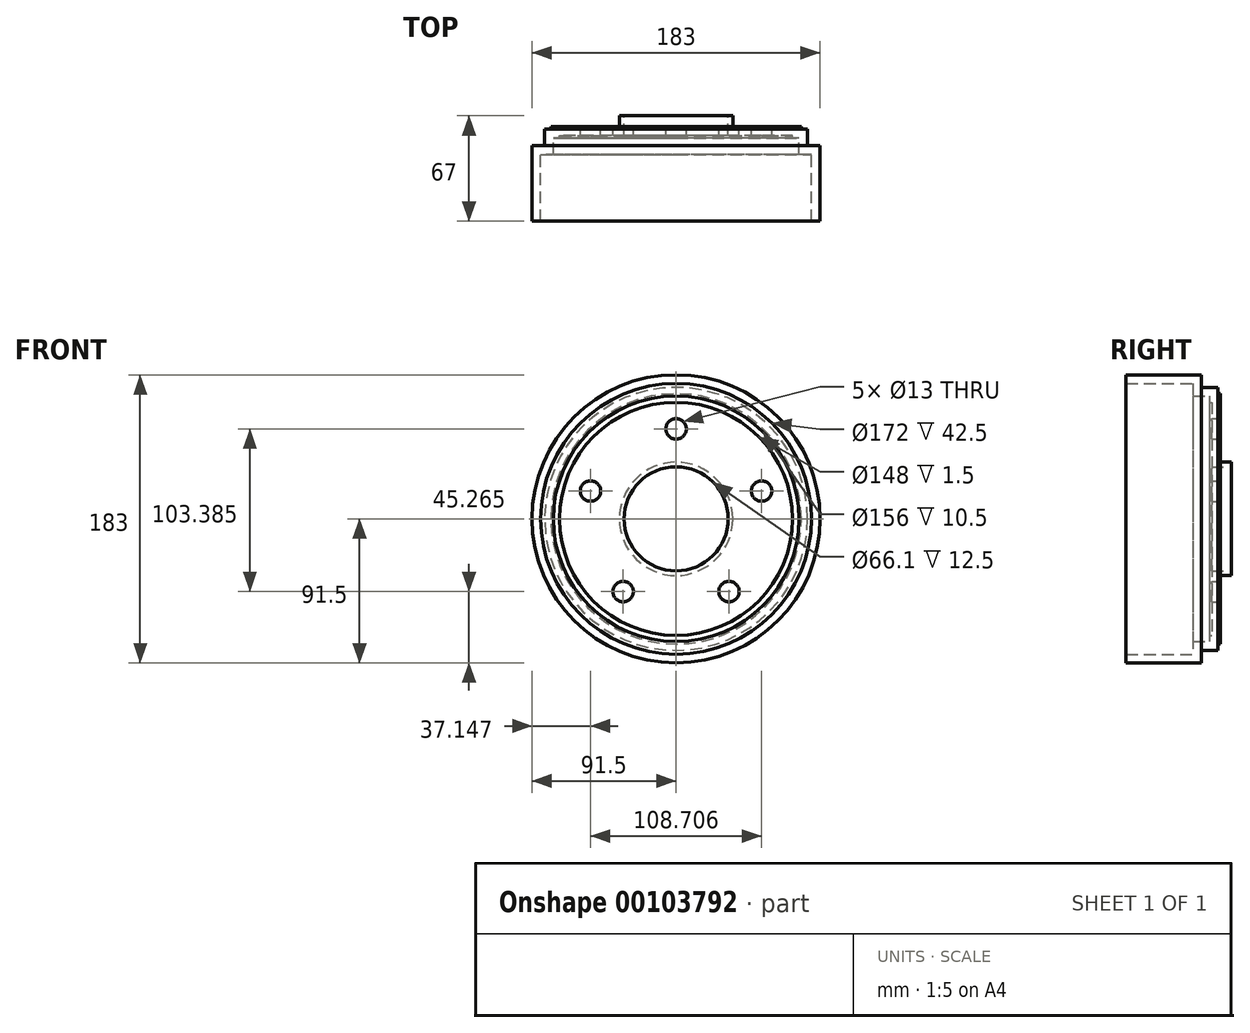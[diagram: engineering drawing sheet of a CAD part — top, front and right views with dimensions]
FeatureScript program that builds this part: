
annotation { "Feature Type Name" : "Feature", "Feature Type Description" : "" }
export const myFeature = defineFeature(function(context is Context, id is Id, definition is map)
    precondition{}
    {
        {
            var Q0;
            Q0=qCreatedBy(makeId("Top.planeOp"),FACE);
            var sketch = newSketch(context, id + "F0", { "sketchPlane" : qUnion([Q0])});
            skLineSegment(sketch, "E0", {"start": v(-86, -71.5) * mm, "end": v(-86, -29) * mm, "construction": true});
            skLineSegment(sketch, "E1", {"start": v(86, -71.5) * mm, "end": v(86, -29) * mm});
            skLineSegment(sketch, "E2", {"start": v(86, -29) * mm, "end": v(78, -29) * mm});
            skLineSegment(sketch, "E3", {"start": v(78, -29) * mm, "end": v(78, -18.5) * mm});
            skLineSegment(sketch, "E4", {"start": v(78, -18.5) * mm, "end": v(74, -18.5) * mm});
            skLineSegment(sketch, "E5", {"start": v(74, -18.5) * mm, "end": v(74, -17) * mm});
            skLineSegment(sketch, "E6", {"start": v(74, -17) * mm, "end": v(30.5, -17) * mm});
            skLineSegment(sketch, "E7", {"start": v(30.5, -17) * mm, "end": v(30.5, -10) * mm});
            skLineSegment(sketch, "E8", {"start": v(30.5, -10) * mm, "end": v(27.55, -10) * mm});
            skLineSegment(sketch, "E9", {"start": v(27.55, -10) * mm, "end": v(27.55, 0) * mm});
            skLineSegment(sketch, "E10", {"start": v(-27.55, 0) * mm, "end": v(-27.55, -10) * mm, "construction": true});
            skLineSegment(sketch, "E11", {"start": v(-27.55, -10) * mm, "end": v(-30.5, -10) * mm, "construction": true});
            skLineSegment(sketch, "E12", {"start": v(-30.5, -10) * mm, "end": v(-30.5, -17) * mm, "construction": true});
            skLineSegment(sketch, "E13", {"start": v(-30.5, -17) * mm, "end": v(-74, -17) * mm, "construction": true});
            skLineSegment(sketch, "E14", {"start": v(-74, -17) * mm, "end": v(-74, -18.5) * mm, "construction": true});
            skLineSegment(sketch, "E15", {"start": v(-74, -18.5) * mm, "end": v(-78, -18.5) * mm, "construction": true});
            skLineSegment(sketch, "E16", {"start": v(-78, -18.5) * mm, "end": v(-78, -29) * mm, "construction": true});
            skLineSegment(sketch, "E17", {"start": v(-78, -29) * mm, "end": v(-86, -29) * mm, "construction": true});
            skLineSegment(sketch, "E18", {"start": v(86, -71.5) * mm, "end": v(91.5, -71.5) * mm});
            skLineSegment(sketch, "E19", {"start": v(91.5, -71.5) * mm, "end": v(91.5, -23.5) * mm});
            skLineSegment(sketch, "E20", {"start": v(91.5, -23.5) * mm, "end": v(83.5, -23.5) * mm});
            skLineSegment(sketch, "E21", {"start": v(83.5, -23.5) * mm, "end": v(83.5, -13) * mm});
            skLineSegment(sketch, "E22", {"start": v(83.5, -13) * mm, "end": v(79.5, -13) * mm});
            skLineSegment(sketch, "E23", {"start": v(79.5, -13) * mm, "end": v(79.5, -11.5) * mm});
            skLineSegment(sketch, "E24", {"start": v(79.5, -11.5) * mm, "end": v(36, -11.5) * mm});
            skLineSegment(sketch, "E25", {"start": v(36, -11.5) * mm, "end": v(36, -4.5) * mm});
            skLineSegment(sketch, "E26", {"start": v(36, -4.5) * mm, "end": v(33.05, -4.5) * mm});
            skLineSegment(sketch, "E27", {"start": v(33.05, -4.5) * mm, "end": v(33.05, 5.5) * mm});
            skLineSegment(sketch, "E28", {"start": v(-33.05, 5.5) * mm, "end": v(-33.05, -4.5) * mm, "construction": true});
            skLineSegment(sketch, "E29", {"start": v(-33.05, -4.5) * mm, "end": v(-36, -4.5) * mm, "construction": true});
            skLineSegment(sketch, "E30", {"start": v(-36, -4.5) * mm, "end": v(-36, -11.5) * mm, "construction": true});
            skLineSegment(sketch, "E31", {"start": v(-36, -11.5) * mm, "end": v(-79.5, -11.5) * mm, "construction": true});
            skLineSegment(sketch, "E32", {"start": v(-79.5, -11.5) * mm, "end": v(-79.5, -13) * mm, "construction": true});
            skLineSegment(sketch, "E33", {"start": v(-79.5, -13) * mm, "end": v(-83.5, -13) * mm, "construction": true});
            skLineSegment(sketch, "E34", {"start": v(-83.5, -13) * mm, "end": v(-83.5, -23.5) * mm, "construction": true});
            skLineSegment(sketch, "E35", {"start": v(-83.5, -23.5) * mm, "end": v(-91.5, -23.5) * mm, "construction": true});
            skLineSegment(sketch, "E36", {"start": v(-91.5, -23.5) * mm, "end": v(-91.5, -71.5) * mm, "construction": true});
            skLineSegment(sketch, "E37", {"start": v(-91.5, -71.5) * mm, "end": v(-86, -71.5) * mm, "construction": true});
            skLineSegment(sketch, "E38", {"start": v(0, 0) * mm, "end": v(27.55, 0) * mm});
            skLineSegment(sketch, "E39", {"start": v(33.05, 5.5) * mm, "end": v(0, 5.5) * mm});
            skLineSegment(sketch, "E40", {"start": v(0, 5.5) * mm, "end": v(0, 0) * mm});
            skLineSegment(sketch, "E41", {"start": v(-27.55, 0) * mm, "end": v(0, 0) * mm, "construction": true});
            skLineSegment(sketch, "E42", {"start": v(-33.05, 5.5) * mm, "end": v(0, 5.5) * mm, "construction": true});
            skSolve(sketch);
        }
        {
            var Q0;
            Q0=makeQuery(id+"F0.imprint","IMPRINT",FACE,{"disambiguationData":[TD([[makeQuery(id+"F0.imprint","IMPRINT",EDGE,{"derivedFrom":sQuery(id+"F0.wireOp",EDGE,"E1")}),-1.0]])]});
            var Q1;
            Q1=sQuery(id+"F0.wireOp",EDGE,"E40");
            revolve(context, id + "F1", {"entities" : qUnion([Q0]), "axis" : qUnion([Q1]), "revolveType" : RevolveType.FULL});
        }
        {
            var Q0;
            Q0=makeQuery(id+"F1.opRevolve","SWEPT_FACE",FACE,{"disambiguationData":[OSD([sQuery(id+"F0.wireOp",EDGE,"E24")])]});
            var sketch = newSketch(context, id + "F2", { "sketchPlane" : qUnion([Q0])});
            skCircle(sketch, "E43", {"center": v(0, 0) * mm, "radius": 57.15 * mm, "construction": true});
            skCircle(sketch, "E44", {"center": v(0, 57.15) * mm, "radius": 6.5 * mm});
            skCircle(sketch, "E45.1.0", {"center": v(-54.35, 17.66) * mm, "radius": 6.5 * mm});
            skCircle(sketch, "E45.2.0", {"center": v(-33.6, -46.24) * mm, "radius": 6.5 * mm});
            skCircle(sketch, "E45.3.0", {"center": v(33.6, -46.24) * mm, "radius": 6.5 * mm});
            skCircle(sketch, "E45.4.0", {"center": v(54.35, 17.66) * mm, "radius": 6.5 * mm});
            skSolve(sketch);
        }
        {
            var Q0;
            Q0 = qSketchRegion(id + "F2", true);
            extrude(context, id + "F3", {"entities" : qUnion([Q0]), "operationType" : NewBodyOperationType.REMOVE, "endBound" : BoundingType.UP_TO_NEXT, "oppositeDirection" : true, "depth" : 25 * mm});
        }
        {
            var Q0;
            Q0=makeQuery(id+"F1.opRevolve","SWEPT_FACE",FACE,{"disambiguationData":[OSD([sQuery(id+"F0.wireOp",EDGE,"E39")])]});
            extrude(context, id + "F4", {"entities" : qUnion([Q0]), "operationType" : NewBodyOperationType.REMOVE, "endBound" : BoundingType.THROUGH_ALL, "oppositeDirection" : true, "depth" : 25 * mm});
        }
    });
